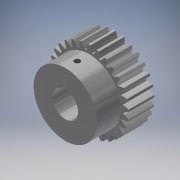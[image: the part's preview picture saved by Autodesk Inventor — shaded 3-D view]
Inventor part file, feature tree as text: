
AUTODESK INVENTOR PART (.ipt)
format: ipt  version: 2019 (Build 230136000, 136)  size: 305,664 bytes
history: native  units: mm (DEFAULTED — no unit token found)
features: sketch x5, plane x4, extrude x3, other x3, hole x1, projected_geometry x1
ambient origin geometry x8: Origin, YZ Plane, XZ Plane, XY Plane, X Axis, Y Axis, Z Axis, Center Point
bodies: Solid1 (feature_tree)
feature tree (17):
  extrude  "Extrusion1"  Depth=15.0mm TaperAngle=0.0deg
  plane  "Work Plane2"
  plane  "Work Plane8"
  plane  "Work Plane9"
  other  "正齒輪"
  extrude  "擠出2"  Depth=10.0mm TaperAngle=0.0deg
  extrude  "擠出3"  Depth=29.0mm
  plane  "工作平面11"
  hole  "孔1"  [1 undecoded]
  sketch  "Sketch1"  dims[d0=46.466966mm d1=15.0mm d2=0.0mm]
  sketch  "Sketch2"  dims[d3=43.889556mm d4=10.0mm d5=0.0mm d16=56.753736mm d17=0.0mm d34=1.083308mm d39=0.0mm d41=0.0mm d43=56.753736mm d46=56.753736mm d47=0.0mm d48=0.0mm d49=15.0mm d50=29.0mm d51=0.0mm d52=37.0mm d53=2.0mm d54=5.0mm d55=2.0mm d56=14.0mm d57=0.0mm d58=3.242mm d59=8.0mm d60=4.0mm d61=2.0mm d62=90.0deg d63=8.0mm d64=20.594885mm]
  other  "Srf1"
  sketch  "草圖3"
  sketch  "草圖4"
  sketch  "草圖5"
  projected_geometry  "投影迴路1"
  other  "節圓直徑"
note: 1 required parameter value undecoded (feature->parameter linkage not recoverable at this tier; creation-order binding heuristic only, values carry confidence <= 0.55)
